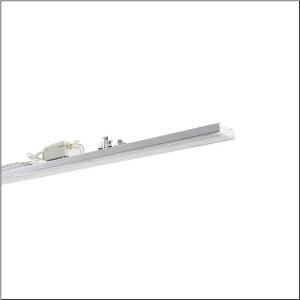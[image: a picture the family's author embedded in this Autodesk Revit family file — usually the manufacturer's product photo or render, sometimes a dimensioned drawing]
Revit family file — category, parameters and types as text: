
# Revit family: licross_21_recessed_mo_52te117n485g
name_source: partatom
category: Lighting Fixtures
units: mm (PartAtom-declared; Revit-internal decimal feet)

## family parameters
Cut with Voids When Loaded = No
Host = Face
Light Source = No
Part Type = Normal
Room Calculation Point = No
Round Connector Dimension = Use Diameter
Shared = No

## types (1)
- Licross 21 Recessed MO (1 x LED, 8680 lm, 47.9 W, 4000K)
    Apparent Load = 48 VA
    CIE Flux Codes = 89 96 99 100 100
    Color Rendering = 80
    Color Temperature = 4000K
    Default Elevation = 1800 mm
    Description = Licross 21 Recessed MO, luminaire insert, of sheet steel, galvanised, coil coated, white, length: 1.500mm, width: 66mm, height: 67mm, LED rated luminous flux: 8.680lm, light colour: 840, SDCM (Standard Deviation of Colour Matching)MacAdam ≤ 3 SDCM (initial), control gear: ON/OFF, with plug, 3-pole, with phase selection, mains connection: 220..240V, AC, 50/60Hz, rated input power: 48W, internal wiring halogen-free, primary light control with lens, of plastic, primary optical cover: cover, of PMMA, light emission: direct distribution, primary light characteristic: symmetric, protection rating (complete): IP54, insulation class (complete): insulation class I (protective earthing), certification: CE, ENEC, VDE, UKCA, protection symbol: D if used in an environment with non-conductive dust loads with corresponding accessories, impact resistance: IK06, permissible ambient temperature for indoor applications: -35..+40°C, corresponds to IFS (International Featured Standards) requirements for safety and quality in the food industry, reducing of maximum allowable ambient temperature of 5°C with ceiling mounting, LABS conformity tested according to VDMA 24364:2018-05, The light source and the operating device comply with the requirements of the Ecodesign Regulation (EU) 2019/2020 and are replaceable in accordance with this regulation, packaging unit: 1 piece
    Height = 58 mm
    Lamp = 1 x LED
    Lamp Light Flux = 8680 lm
    Lamp Power = 47.9 W
    Lamp count = 1
    Length = 1500 mm
    Luminous efficacy = 181 lm/W
    Manufacturer = Siteco
    ModVariant = No
    Model = 52TE117N485G
    Mounting Place = Ceiling
    Mounting Type = Pendant
    Number of Poles = 1
    OnlyDefault = Yes
    Power Factor = 1
    Product Name = Licross 21 Recessed MO
    Product group = luminaire insert | ceiling pendant
    ProductGroupID = 901
    Protection Class = Protection class I
    Protection Degree = IP 54
    RLX_Detail_Level = 1
    RLX_Emergency_Light_Flux = 0 lm
    RLX_Emergency_Type = 0
    RLX_Emergency_Type_DB = No
    RlxData = <blob elided: 21117 chars, md5=dc4d3e2c>
    Socket = socket
    Standby Power = 0 W
    System Light Flux = 8680 lm
    System Power = 48 W
    Type Comments = Product without accessories
    Type Image = l_1296930.jpg
    URL = http://relux.com
    VarID = ---
    Voltage = 0 V
    Weight = 0.00 kg
    Width = 66 mm

## geometry (parser evidence)
native form markers: Blend x4, Sweep x11
no freeform markers — native parametric forms only
